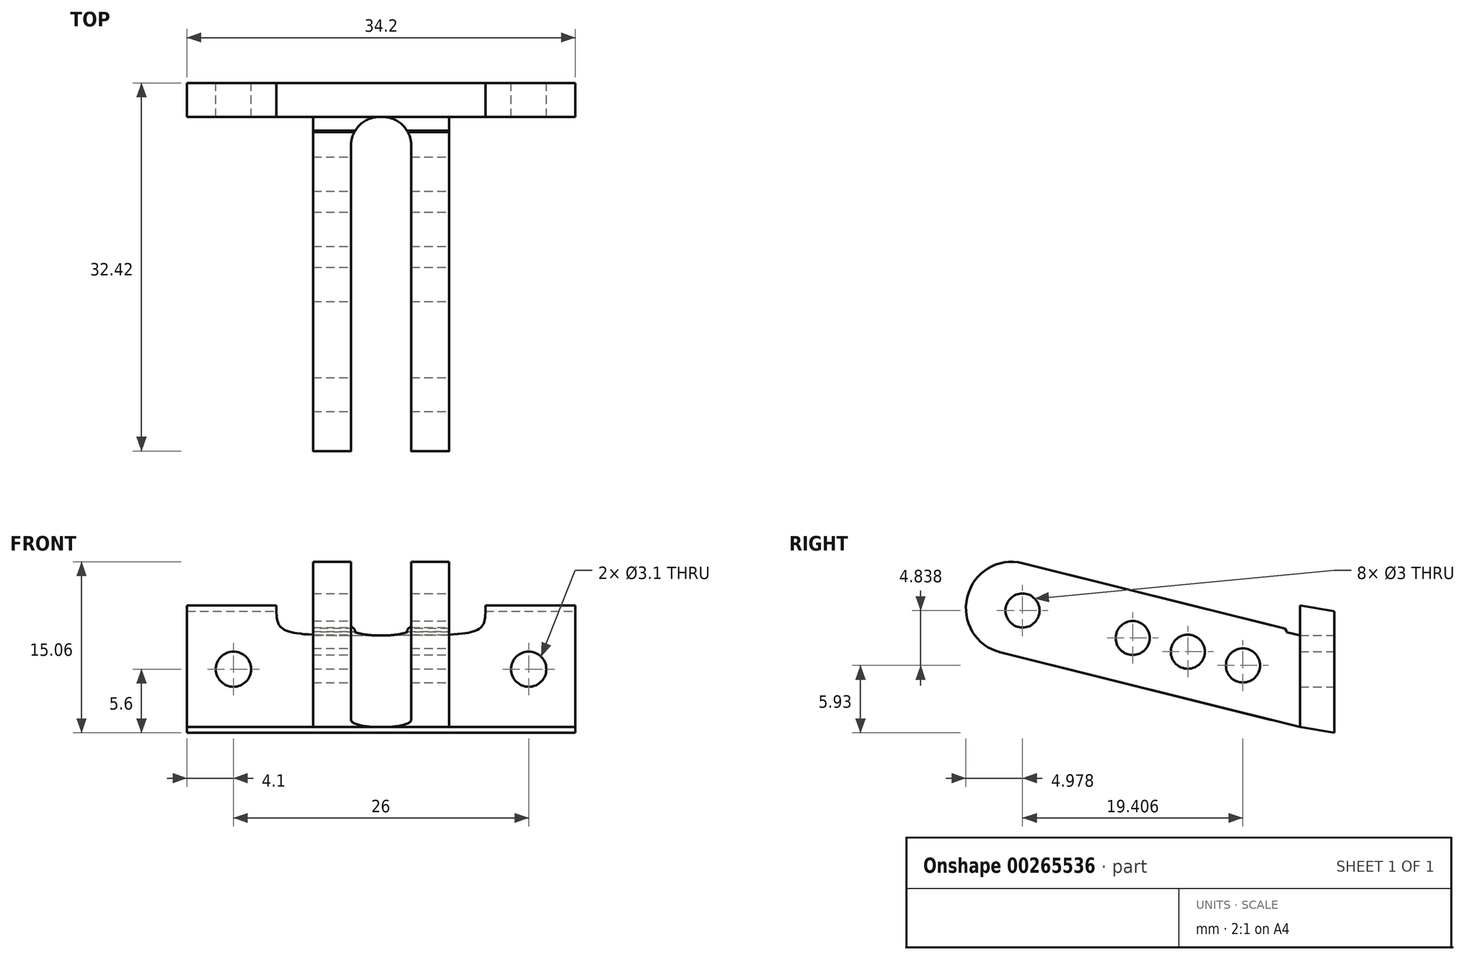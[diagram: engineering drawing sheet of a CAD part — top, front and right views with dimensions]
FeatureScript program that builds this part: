
annotation { "Feature Type Name" : "Feature", "Feature Type Description" : "" }
export const myFeature = defineFeature(function(context is Context, id is Id, definition is map)
    precondition{}
    {
        {
            var Q0;
            Q0=qCreatedBy(makeId("Front.planeOp"),FACE);
            var sketch = newSketch(context, id + "F0", { "sketchPlane" : qUnion([Q0])});
            skLineSegment(sketch, "E0.bottom", {"start": v(-17.1, -5.6) * mm, "end": v(17.1, -5.6) * mm});
            skLineSegment(sketch, "E0.top", {"start": v(-17.1, 5.6) * mm, "end": v(17.1, 5.6) * mm});
            skLineSegment(sketch, "E0.left", {"start": v(-17.1, -5.6) * mm, "end": v(-17.1, 5.6) * mm});
            skLineSegment(sketch, "E0.right", {"start": v(17.1, -5.6) * mm, "end": v(17.1, 5.6) * mm});
            skPoint(sketch, "E0.middle", {"position": v(0, 0) * mm});
            skFitSpline(sketch, "E1", {"points": [v(-9.22, 5.6) * mm, v(-0.02, 2.97) * mm], "startDerivative": vector(0, -7.9) * mm, "endDerivative": vector(27.6, 0) * mm});
            skFitSpline(sketch, "E2", {"points": [v(9.18, 5.6) * mm, v(-0.02, 2.97) * mm], "startDerivative": vector(0, -7.9) * mm, "endDerivative": vector(-27.6, 0) * mm});
            skLineSegment(sketch, "E3", {"start": v(0, 0) * mm, "end": v(0, -10.28) * mm, "construction": true});
            skLineSegment(sketch, "E4", {"start": v(0, 0) * mm, "end": v(-13, 0) * mm, "construction": true});
            skCircle(sketch, "E5", {"center": v(-13, 0) * mm, "radius": 1.55 * mm});
            skCircle(sketch, "E6.MirrorC", {"center": v(13, 0) * mm, "radius": 1.55 * mm});
            skSolve(sketch);
        }
        {
            var Q0;
            Q0=makeQuery(id+"F0.imprint","IMPRINT",FACE,{"disambiguationData":[TD([[makeQuery(id+"F0.imprint","IMPRINT",EDGE,{"derivedFrom":sQuery(id+"F0.wireOp",EDGE,"E0.bottom")}),1.0]])]});
            extrude(context, id + "F1", {"entities" : qUnion([Q0]), "depth" : 3 * mm});
        }
        {
            var Q0;
            {var subQ0=sQuery(id+"F0.wireOp",EDGE,"E0.top");Q0=makeQuery(id+"F1.opExtrude","CAP_EDGE",EDGE,{"disambiguationData":[OSD([subQ0]),TDD([makeQuery(id+"F0.imprint","IMPRINT",EDGE,{"disambiguationData":[TD([[makeQuery(id+"F0.imprint","INTERSECT",VERTEX,{"derivedFrom":[subQ0,sQuery(id+"F0.wireOp",EDGE,"E0.left")]}),-1.0]])],"derivedFrom":subQ0})])],"isStart":true});}
            var Q1;
            {var subQ0=sQuery(id+"F0.wireOp",EDGE,"E0.top");Q1=makeQuery(id+"F1.opExtrude","CAP_EDGE",EDGE,{"disambiguationData":[OSD([subQ0]),TDD([makeQuery(id+"F0.imprint","IMPRINT",EDGE,{"disambiguationData":[TD([[makeQuery(id+"F0.imprint","INTERSECT",VERTEX,{"derivedFrom":[subQ0,sQuery(id+"F0.wireOp",EDGE,"E0.right")]}),1.0]])],"derivedFrom":subQ0})])],"isStart":true});}
            var Q2;
            Q2=makeQuery(id+"F1.opExtrude","CAP_EDGE",EDGE,{"disambiguationData":[OSD([sQuery(id+"F0.wireOp",EDGE,"E0.bottom")])],"isStart":false});
            chamfer(context, id + "F2", {"entities" : qUnion([Q0, Q1, Q2]), "chamferType" : ChamferType.TWO_OFFSETS, "width1" : 0.5 * mm, "oppositeDirection" : false, "width2" : 3 * mm, "tangentPropagation" : true});
        }
        {
            var Q0;
            Q0=qCreatedBy(makeId("Right.planeOp"),FACE);
            var sketch = newSketch(context, id + "F3", { "sketchPlane" : qUnion([Q0])});
            skLineSegment(sketch, "E7", {"start": v(-3, -5.1) * mm, "end": v(-33.27, 2.45) * mm});
            skLineSegment(sketch, "E8", {"start": v(-33.27, 2.45) * mm, "end": v(-31.31, 10.3) * mm});
            skLineSegment(sketch, "E9", {"start": v(-31.31, 10.3) * mm, "end": v(-4.15, 3.53) * mm});
            skLineSegment(sketch, "E10", {"start": v(-3, 2.97) * mm, "end": v(-4.21, 3.27) * mm});
            skLineSegment(sketch, "E11", {"start": v(-4.15, 3.53) * mm, "end": v(-4.21, 3.27) * mm});
            skLineSegment(sketch, "E12", {"start": v(-3, -5.1) * mm, "end": v(-3, 2.97) * mm});
            skSolve(sketch);
        }
        {
            var Q0;
            Q0=makeQuery(id+"F3.imprint","IMPRINT",FACE,{"disambiguationData":[TD([[makeQuery(id+"F3.imprint","IMPRINT",EDGE,{"derivedFrom":sQuery(id+"F3.wireOp",EDGE,"E7")}),-1.0]])]});
            extrude(context, id + "F4", {"entities" : qUnion([Q0]), "operationType" : NewBodyOperationType.ADD, "depth" : 6 * mm});
        }
        {
            var Q0;
            Q0=makeQuery(id+"F4.opExtrude","CAP_FACE",FACE,{"disambiguationData":[OSD([sQuery(id+"F3.wireOp",EDGE,"E7"),sQuery(id+"F3.wireOp",EDGE,"E8"),sQuery(id+"F3.wireOp",EDGE,"E9"),sQuery(id+"F3.wireOp",EDGE,"E10"),sQuery(id+"F3.wireOp",EDGE,"E11"),sQuery(id+"F3.wireOp",EDGE,"E12")])],"isStart":true});
            extrude(context, id + "F5", {"entities" : qUnion([Q0]), "operationType" : NewBodyOperationType.ADD, "depth" : 6 * mm});
        }
        {
            var Q0;
            Q0=makeQuery(id+"F4.opExtrude","CAP_FACE",FACE,{"disambiguationData":[OSD([sQuery(id+"F3.wireOp",EDGE,"E7"),sQuery(id+"F3.wireOp",EDGE,"E8"),sQuery(id+"F3.wireOp",EDGE,"E9"),sQuery(id+"F3.wireOp",EDGE,"E10"),sQuery(id+"F3.wireOp",EDGE,"E11"),sQuery(id+"F3.wireOp",EDGE,"E12")])],"isStart":false});
            var sketch = newSketch(context, id + "F6", { "sketchPlane" : qUnion([Q0])});
            skLineSegment(sketch, "E13", {"start": v(-32.3, 6.38) * mm, "end": v(-27.44, 5.17) * mm, "construction": true});
            skCircle(sketch, "E14", {"center": v(-27.44, 5.17) * mm, "radius": 1.5 * mm});
            skLineSegment(sketch, "E15", {"start": v(-27.44, 5.17) * mm, "end": v(-17.74, 2.75) * mm, "construction": true});
            skCircle(sketch, "E16", {"center": v(-17.74, 2.75) * mm, "radius": 1.5 * mm});
            skLineSegment(sketch, "E17", {"start": v(-17.74, 2.75) * mm, "end": v(-12.89, 1.54) * mm, "construction": true});
            skCircle(sketch, "E18", {"center": v(-12.89, 1.54) * mm, "radius": 1.5 * mm});
            skLineSegment(sketch, "E19", {"start": v(-12.89, 1.54) * mm, "end": v(-8.04, 0.33) * mm, "construction": true});
            skCircle(sketch, "E20", {"center": v(-8.04, 0.33) * mm, "radius": 1.5 * mm});
            skSolve(sketch);
        }
        {
            var Q0;
            Q0=makeQuery(id+"F6.imprint","IMPRINT",FACE,{"disambiguationData":[TD([[makeQuery(id+"F6.imprint","IMPRINT",EDGE,{"derivedFrom":sQuery(id+"F6.wireOp",EDGE,"E14")}),1.0]])]});
            var Q1;
            Q1=makeQuery(id+"F6.imprint","IMPRINT",FACE,{"disambiguationData":[TD([[makeQuery(id+"F6.imprint","IMPRINT",EDGE,{"derivedFrom":sQuery(id+"F6.wireOp",EDGE,"E16")}),1.0]])]});
            var Q2;
            Q2=makeQuery(id+"F6.imprint","IMPRINT",FACE,{"disambiguationData":[TD([[makeQuery(id+"F6.imprint","IMPRINT",EDGE,{"derivedFrom":sQuery(id+"F6.wireOp",EDGE,"E18")}),1.0]])]});
            var Q3;
            Q3=makeQuery(id+"F6.imprint","IMPRINT",FACE,{"disambiguationData":[TD([[makeQuery(id+"F6.imprint","IMPRINT",EDGE,{"derivedFrom":sQuery(id+"F6.wireOp",EDGE,"E20")}),1.0]])]});
            extrude(context, id + "F7", {"entities" : qUnion([Q0, Q1, Q2, Q3]), "operationType" : NewBodyOperationType.REMOVE, "oppositeDirection" : true, "depth" : 25 * mm});
        }
        {
            var Q0;
            {var subQ0=sQuery(id+"F0.wireOp",EDGE,"E0.bottom");Q0=makeQuery(id+"F2.opChamfer","BLEND_EDGE",EDGE,{"blendedFrom":[makeQuery(id+"F1.opExtrude","CAP_EDGE",EDGE,{"disambiguationData":[OSD([subQ0])],"isStart":false}),makeQuery(id+"F1.opExtrude","CAP_FACE",FACE,{"disambiguationData":[OSD([subQ0,sQuery(id+"F0.wireOp",EDGE,"E0.top"),sQuery(id+"F0.wireOp",EDGE,"E0.left"),sQuery(id+"F0.wireOp",EDGE,"E0.right"),sQuery(id+"F0.wireOp",EDGE,"E1"),sQuery(id+"F0.wireOp",EDGE,"E2"),sQuery(id+"F0.wireOp",EDGE,"E5"),sQuery(id+"F0.wireOp",EDGE,"E6.MirrorC")])],"isStart":true})],"blendedInto":[makeQuery(id+"F1.opExtrude","CAP_FACE",FACE,{"disambiguationData":[OSD([subQ0,sQuery(id+"F0.wireOp",EDGE,"E0.top"),sQuery(id+"F0.wireOp",EDGE,"E0.left"),sQuery(id+"F0.wireOp",EDGE,"E0.right"),sQuery(id+"F0.wireOp",EDGE,"E1"),sQuery(id+"F0.wireOp",EDGE,"E2"),sQuery(id+"F0.wireOp",EDGE,"E5"),sQuery(id+"F0.wireOp",EDGE,"E6.MirrorC")])],"isStart":true})]});}
            cPlane(context, id + "F8", {"entities" : qUnion([Q0]), "cplaneType" : CPlaneType.LINE_ANGLE, "offset" : 25 * mm, "angle" : 90 * degree, "oppositeDirection" : true, "width" : 150 * mm, "height" : 150 * mm});
        }
        {
            var Q0;
            Q0=qCreatedBy(id+"F8.planeOp",FACE);
            var sketch = newSketch(context, id + "F9", { "sketchPlane" : qUnion([Q0])});
            skLineSegment(sketch, "E21.bottom", {"start": v(-2.65, 3) * mm, "end": v(2.65, 3) * mm});
            skLineSegment(sketch, "E21.top", {"start": v(-2.65, 33.27) * mm, "end": v(2.65, 33.27) * mm});
            skLineSegment(sketch, "E21.left", {"start": v(-2.65, 3) * mm, "end": v(-2.65, 33.27) * mm});
            skLineSegment(sketch, "E21.right", {"start": v(2.65, 3) * mm, "end": v(2.65, 33.27) * mm});
            skSolve(sketch);
        }
        {
            var Q0;
            Q0 = qSketchRegion(id + "F9", true);
            extrude(context, id + "F10", {"entities" : qUnion([Q0]), "operationType" : NewBodyOperationType.REMOVE, "oppositeDirection" : true, "depth" : 25 * mm});
        }
        {
            var Q0;
            {var subQ0=sQuery(id+"F3.wireOp",EDGE,"E7");var subQ1=sQuery(id+"F3.wireOp",EDGE,"E8");Q0=makeQuery(id+"F10.boolean.opBoolean","SPLIT",EDGE,{"disambiguationData":[TD([makeQuery(id+"F10.opExtrude","SWEPT_FACE",FACE,{"disambiguationData":[OSD([sQuery(id+"F9.wireOp",EDGE,"E21.left")])]})])],"derivedFrom":makeQuery(id+"F5.boolean.opBoolean","MERGE",EDGE,{"derivedFrom":[makeQuery(id+"F4.opExtrude","SWEPT_EDGE",EDGE,{"disambiguationData":[OSD([subQ0,subQ1])]}),makeQuery(id+"F5.opExtrude","SWEPT_EDGE",EDGE,{"disambiguationData":[OSD([subQ0,subQ1])]})]})});}
            var Q1;
            {var subQ0=sQuery(id+"F3.wireOp",EDGE,"E8");var subQ1=sQuery(id+"F3.wireOp",EDGE,"E7");Q1=makeQuery(id+"F10.boolean.opBoolean","SPLIT",EDGE,{"disambiguationData":[TD([makeQuery(id+"F10.opExtrude","SWEPT_FACE",FACE,{"disambiguationData":[OSD([sQuery(id+"F9.wireOp",EDGE,"E21.right")])]})])],"derivedFrom":makeQuery(id+"F5.boolean.opBoolean","MERGE",EDGE,{"derivedFrom":[makeQuery(id+"F4.opExtrude","SWEPT_EDGE",EDGE,{"disambiguationData":[OSD([subQ1,subQ0])]}),makeQuery(id+"F5.opExtrude","SWEPT_EDGE",EDGE,{"disambiguationData":[OSD([subQ1,subQ0])]})]})});}
            var Q2;
            {var subQ0=sQuery(id+"F3.wireOp",EDGE,"E9");var subQ1=sQuery(id+"F3.wireOp",EDGE,"E8");Q2=makeQuery(id+"F10.boolean.opBoolean","SPLIT",EDGE,{"disambiguationData":[TD([makeQuery(id+"F10.opExtrude","SWEPT_FACE",FACE,{"disambiguationData":[OSD([sQuery(id+"F9.wireOp",EDGE,"E21.left")])]})])],"derivedFrom":makeQuery(id+"F5.boolean.opBoolean","MERGE",EDGE,{"derivedFrom":[makeQuery(id+"F4.opExtrude","SWEPT_EDGE",EDGE,{"disambiguationData":[OSD([subQ1,subQ0])]}),makeQuery(id+"F5.opExtrude","SWEPT_EDGE",EDGE,{"disambiguationData":[OSD([subQ1,subQ0])]})]})});}
            var Q3;
            {var subQ0=sQuery(id+"F3.wireOp",EDGE,"E9");var subQ1=sQuery(id+"F3.wireOp",EDGE,"E8");Q3=makeQuery(id+"F10.boolean.opBoolean","SPLIT",EDGE,{"disambiguationData":[TD([makeQuery(id+"F10.opExtrude","SWEPT_FACE",FACE,{"disambiguationData":[OSD([sQuery(id+"F9.wireOp",EDGE,"E21.right")])]})])],"derivedFrom":makeQuery(id+"F5.boolean.opBoolean","MERGE",EDGE,{"derivedFrom":[makeQuery(id+"F4.opExtrude","SWEPT_EDGE",EDGE,{"disambiguationData":[OSD([subQ1,subQ0])]}),makeQuery(id+"F5.opExtrude","SWEPT_EDGE",EDGE,{"disambiguationData":[OSD([subQ1,subQ0])]})]})});}
            fillet(context, id + "F11", {"entities" : qUnion([Q0, Q1, Q2, Q3]), "radius" : 4 * mm, "tangentPropagation" : true, "allowEdgeOverflow" : false});
        }
        {
            var Q0;
            Q0=makeQuery(id+"F10.boolean.opBoolean","COPY",EDGE,{"derivedFrom":makeQuery(id+"F10.opExtrude","SWEPT_EDGE",EDGE,{"disambiguationData":[OSD([sQuery(id+"F9.wireOp",EDGE,"E21.bottom"),sQuery(id+"F9.wireOp",EDGE,"E21.left")])]})});
            var Q1;
            Q1=makeQuery(id+"F10.boolean.opBoolean","COPY",EDGE,{"derivedFrom":makeQuery(id+"F10.opExtrude","SWEPT_EDGE",EDGE,{"disambiguationData":[OSD([sQuery(id+"F9.wireOp",EDGE,"E21.bottom"),sQuery(id+"F9.wireOp",EDGE,"E21.right")])]})});
            fillet(context, id + "F12", {"entities" : qUnion([Q0, Q1]), "radius" : 2.5 * mm, "tangentPropagation" : true, "allowEdgeOverflow" : false});
        }
        {
            var Q0;
            {var subQ0=sQuery(id+"F3.wireOp",EDGE,"E11");var subQ1=sQuery(id+"F3.wireOp",EDGE,"E9");Q0=makeQuery(id+"F10.boolean.opBoolean","SPLIT",EDGE,{"disambiguationData":[TD([makeQuery(id+"F10.opExtrude","SWEPT_FACE",FACE,{"disambiguationData":[OSD([sQuery(id+"F9.wireOp",EDGE,"E21.right")])]})])],"derivedFrom":makeQuery(id+"F5.boolean.opBoolean","MERGE",EDGE,{"derivedFrom":[makeQuery(id+"F4.opExtrude","SWEPT_EDGE",EDGE,{"disambiguationData":[OSD([subQ1,subQ0])]}),makeQuery(id+"F5.opExtrude","SWEPT_EDGE",EDGE,{"disambiguationData":[OSD([subQ1,subQ0])]})]})});}
            var Q1;
            {var subQ0=sQuery(id+"F3.wireOp",EDGE,"E11");var subQ1=sQuery(id+"F3.wireOp",EDGE,"E9");Q1=makeQuery(id+"F10.boolean.opBoolean","SPLIT",EDGE,{"disambiguationData":[TD([makeQuery(id+"F10.opExtrude","SWEPT_FACE",FACE,{"disambiguationData":[OSD([sQuery(id+"F9.wireOp",EDGE,"E21.left")])]})])],"derivedFrom":makeQuery(id+"F5.boolean.opBoolean","MERGE",EDGE,{"derivedFrom":[makeQuery(id+"F4.opExtrude","SWEPT_EDGE",EDGE,{"disambiguationData":[OSD([subQ1,subQ0])]}),makeQuery(id+"F5.opExtrude","SWEPT_EDGE",EDGE,{"disambiguationData":[OSD([subQ1,subQ0])]})]})});}
            chamfer(context, id + "F13", {"entities" : qUnion([Q0, Q1]), "width" : 0.2 * mm, "tangentPropagation" : true});
        }
    });
